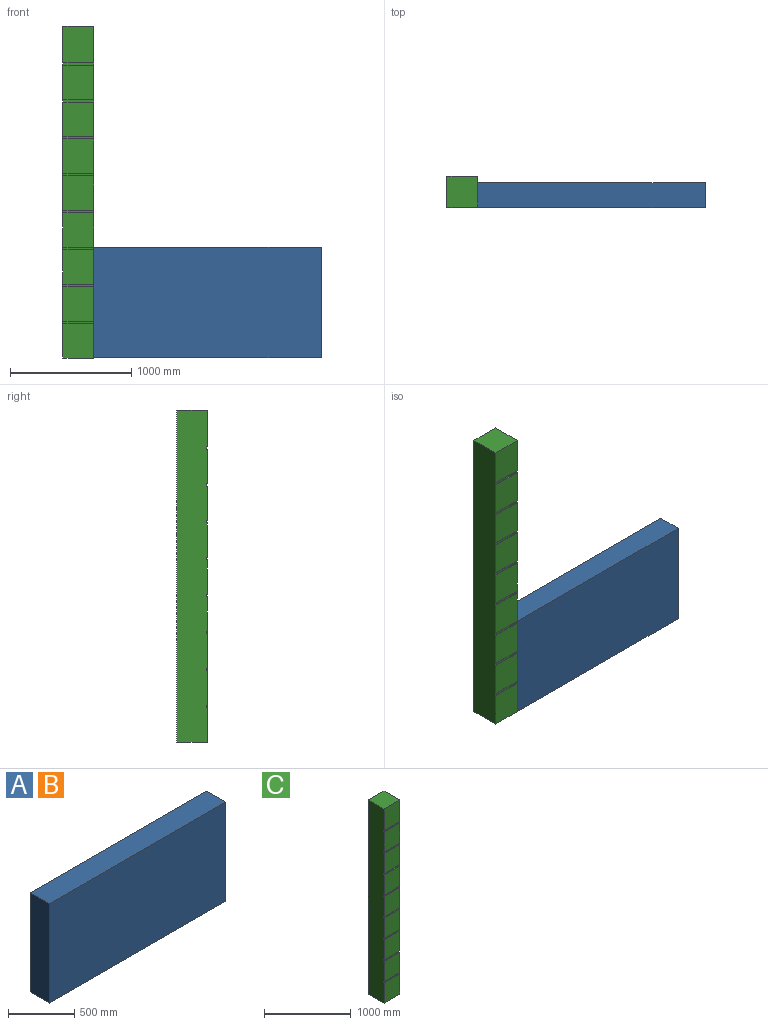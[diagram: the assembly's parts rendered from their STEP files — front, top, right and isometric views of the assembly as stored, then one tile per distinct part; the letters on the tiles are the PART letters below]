
ASSEMBLY  parts=3 mates=1
PART A: 6 faces, bbox 1879.6x203.2x914.4 mm
  f0: plane 1879.6x203.2mm, normal (0,0,1), area 381934.7mm2, adj f1,f3,f4,f5
  f1: plane 1879.6x914.4mm, normal (0,-1,0), area 1718706.2mm2, adj f0,f2,f4,f5
  f2: plane 1879.6x203.2mm, normal (0,0,-1), area 381934.7mm2, adj f1,f3,f4,f5
  f3: plane 1879.6x914.4mm, normal (0,1,0), area 1718706.2mm2, adj f0,f2,f4,f5
  f4: plane 914.4x203.2mm, normal (1,0,0), area 185806.1mm2, adj f0,f1,f2,f3
  f5: plane 914.4x203.2mm, normal (-1,0,0), area 185806.1mm2, adj f0,f1,f2,f3
PART B: same geometry as A
PART C: 38 faces, bbox 254x254x2743.2 mm
  f0: plane 285.75x254mm, normal (0,-1,0), area 72580.5mm2, adj f6,f10,f32,f36
  f1: plane 285.75x254mm, normal (0,-1,0), area 72580.5mm2, adj f6,f10,f29,f33
  f2: plane 285.75x254mm, normal (0,-1,0), area 72580.5mm2, adj f6,f10,f26,f30
  f3: plane 285.75x254mm, normal (0,-1,0), area 72580.5mm2, adj f6,f10,f23,f27
  f4: plane 285.75x254mm, normal (0,-1,0), area 72580.5mm2, adj f6,f10,f20,f24
  f5: plane 285.75x254mm, normal (0,-1,0), area 72580.5mm2, adj f6,f10,f13,f21
  f6: plane 2743.2x254mm, normal (1,0,0), area 695805.1mm2, adj f0,f1,f2,f3,f4,f5,f7,f8
  f7: plane 285.75x254mm, normal (0,-1,0), area 72580.5mm2, adj f6,f10,f18,f35
  f8: plane 285.75x254mm, normal (0,-1,0), area 72580.5mm2, adj f6,f10,f15,f17
  f9: plane 2743.2x254mm, normal (0,1,0), area 696772.8mm2, adj f6,f10,f12,f13
  f10: plane 2743.2x254mm, normal (-1,0,0), area 695805.1mm2, adj f0,f1,f2,f3,f4,f5,f7,f8
  f11: plane 304.8x254mm, normal (0,-1,0), area 77419.2mm2, adj f6,f10,f12,f14
  f12: plane 254x254mm, normal (0,0,1), area 64516mm2, adj f6,f9,f10,f11
  f13: plane 254x254mm, normal (0,0,-1), area 64516mm2, adj f5,f6,f9,f10
  f14: plane 254x6.35mm, normal (0,0,-1), area 1612.9mm2, adj f6,f10,f11,f16
  f15: plane 254x6.35mm, normal (0,0,1), area 1612.9mm2, adj f6,f8,f10,f16
  f16: plane 254x19.05mm, normal (0,-1,0), area 4838.7mm2, adj f6,f10,f14,f15
  f17: plane 254x6.35mm, normal (0,0,-1), area 1612.9mm2, adj f6,f8,f10,f19
  f18: plane 254x6.35mm, normal (0,0,1), area 1612.9mm2, adj f6,f7,f10,f19
  f19: plane 254x19.05mm, normal (0,-1,0), area 4838.7mm2, adj f6,f10,f17,f18
  f20: plane 254x6.35mm, normal (0,0,-1), area 1612.9mm2, adj f4,f6,f10,f22
  f21: plane 254x6.35mm, normal (0,0,1), area 1612.9mm2, adj f5,f6,f10,f22
  f22: plane 254x19.05mm, normal (0,-1,0), area 4838.7mm2, adj f6,f10,f20,f21
  f23: plane 254x6.35mm, normal (0,0,-1), area 1612.9mm2, adj f3,f6,f10,f25
  f24: plane 254x6.35mm, normal (0,0,1), area 1612.9mm2, adj f4,f6,f10,f25
  f25: plane 254x19.05mm, normal (0,-1,0), area 4838.7mm2, adj f6,f10,f23,f24
  f26: plane 254x6.35mm, normal (0,0,-1), area 1612.9mm2, adj f2,f6,f10,f28
  f27: plane 254x6.35mm, normal (0,0,1), area 1612.9mm2, adj f3,f6,f10,f28
  f28: plane 254x19.05mm, normal (0,-1,0), area 4838.7mm2, adj f6,f10,f26,f27
  f29: plane 254x6.35mm, normal (0,0,-1), area 1612.9mm2, adj f1,f6,f10,f31
  f30: plane 254x6.35mm, normal (0,0,1), area 1612.9mm2, adj f2,f6,f10,f31
  f31: plane 254x19.05mm, normal (0,-1,0), area 4838.7mm2, adj f6,f10,f29,f30
  f32: plane 254x6.35mm, normal (0,0,-1), area 1612.9mm2, adj f0,f6,f10,f34
  f33: plane 254x6.35mm, normal (0,0,1), area 1612.9mm2, adj f1,f6,f10,f34
  f34: plane 254x19.05mm, normal (0,-1,0), area 4838.7mm2, adj f6,f10,f32,f33
  f35: plane 254x6.35mm, normal (0,0,-1), area 1612.9mm2, adj f6,f7,f10,f37
  f36: plane 254x6.35mm, normal (0,0,1), area 1612.9mm2, adj f0,f6,f10,f37
  f37: plane 254x19.05mm, normal (0,-1,0), area 4838.7mm2, adj f6,f10,f35,f36
PLACE A t=(-1608.2,3222.41,5912.24)mm
PLACE B t=(-1608.2,3222.41,5912.24)mm
PLACE C t=(3380.19,334.75,211.4)mm
MATE fastened C.f6 <-> B.f5  axis (1,0,0) through (-1608.2,-41.77,211.4)mm
